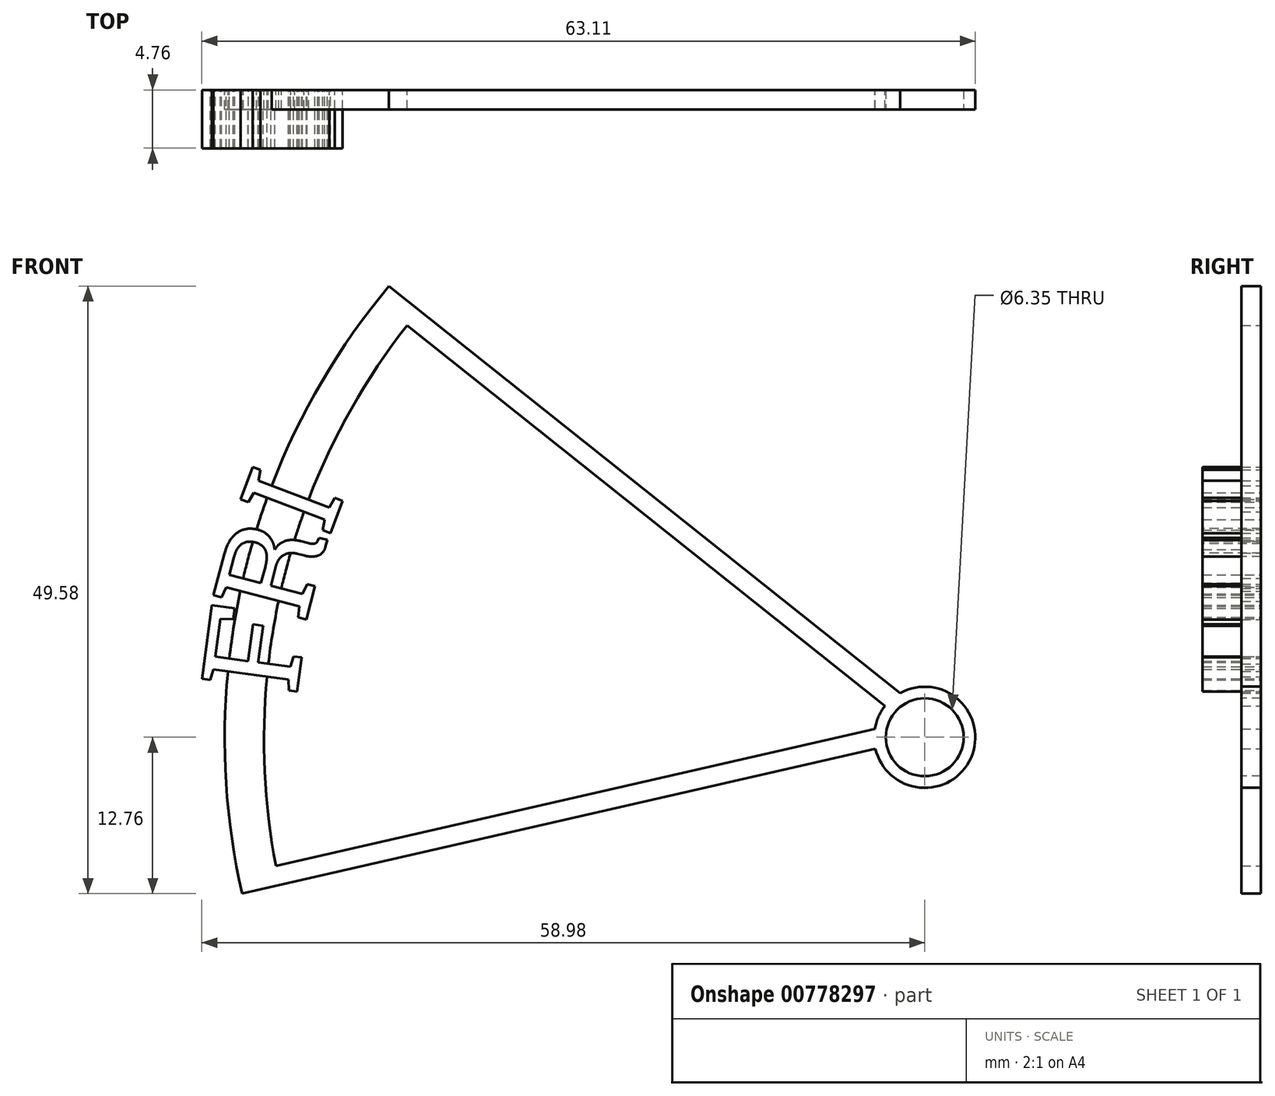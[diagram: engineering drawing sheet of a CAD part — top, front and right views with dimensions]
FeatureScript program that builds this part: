
annotation { "Feature Type Name" : "Feature", "Feature Type Description" : "" }
export const myFeature = defineFeature(function(context is Context, id is Id, definition is map)
    precondition{}
    {
        {
            var Q0;
            Q0=qCreatedBy(makeId("Front.planeOp"),FACE);
            var sketch = newSketch(context, id + "F0", { "sketchPlane" : qUnion([Q0])});
            skCircle(sketch, "E0", {"center": v(0, 0) * mm, "radius": 59.18 * mm, "construction": true});
            skCircle(sketch, "E1", {"center": v(0, 0) * mm, "radius": 50.8 * mm, "construction": true});
            skLineSegment(sketch, "E2", {"start": v(0, 0) * mm, "end": v(0, 59.18) * mm, "construction": true});
            skLineSegment(sketch, "E3", {"start": v(0, 0) * mm, "end": v(-57.83, -12.6) * mm, "construction": true});
            skLineSegment(sketch, "E4", {"start": v(0, 0) * mm, "end": v(-58.65, 7.93) * mm, "construction": true});
            skLineSegment(sketch, "E5", {"start": v(0, 0) * mm, "end": v(-57.24, 15.02) * mm, "construction": true});
            skLineSegment(sketch, "E6", {"start": v(0, 0) * mm, "end": v(-55.36, 20.92) * mm, "construction": true});
            skText(sketch, "E7", { "text": "F", "fontName": "RobotoSlab-Regular.ttf"});
            skText(sketch, "E8", { "text": "R", "fontName": "RobotoSlab-Regular.ttf"});
            skText(sketch, "E9", { "text": "I", "fontName": "RobotoSlab-Regular.ttf"});
            skLineSegment(sketch, "E10", {"start": v(0, 0) * mm, "end": v(-59.13, 4.4) * mm, "construction": true});
            skLineSegment(sketch, "E11", {"start": v(0, 0) * mm, "end": v(-54.67, 22.74) * mm, "construction": true});
            skLineSegment(sketch, "E12", {"start": v(0, 0) * mm, "end": v(-45.9, 37.35) * mm, "construction": true});
            const initialGuessF0  = {"E7": [-0.05126, 0.00334, 0.13406, 0.99097, 0.00794], "E8": [-0.05055, 0.00924, 0.25383, 0.96725, 0.00794], "E9": [-0.04862, 0.0163, 0.35354, 0.93542, 0.00794]};
            skSetInitialGuess(sketch, initialGuessF0);
            skSolve(sketch);
        }
        {
            var Q0;
            Q0=qSketchRegion(id+"F0",true);
            extrude(context, id + "F1", {"entities" : qUnion([Q0]), "depth" : 4.76 * mm, "offsetDistance" : 25.4 * mm});
        }
        {
            var Q0;
            Q0=qCreatedBy(makeId("Front.planeOp"),FACE);
            var sketch = newSketch(context, id + "F2", { "sketchPlane" : qUnion([Q0])});
            skCircle(sketch, "E13", {"center": v(0, 0) * mm, "radius": 57.15 * mm, "construction": true});
            skCircle(sketch, "E14", {"center": v(0, 0) * mm, "radius": 53.98 * mm, "construction": true});
            skCircle(sketch, "E15", {"center": v(0, 0) * mm, "radius": 4.13 * mm, "construction": true});
            skLineSegment(sketch, "E16", {"start": v(0, 0) * mm, "end": v(0, 57.15) * mm, "construction": true});
            skLineSegment(sketch, "E17", {"start": v(0, 0) * mm, "end": v(-55.7, -12.76) * mm, "construction": true});
            skLineSegment(sketch, "E18", {"start": v(0, 0) * mm, "end": v(-42.23, 33.61) * mm, "construction": true});
            skLineSegment(sketch, "E19", {"start": v(-43.7, 36.82) * mm, "end": v(-2, 3.61) * mm, "construction": true});
            skLineSegment(sketch, "E20", {"start": v(-52.94, -10.5) * mm, "end": v(-4.07, 0.7) * mm, "construction": true});
            skLineSegment(sketch, "E21", {"start": v(-42.23, 33.61) * mm, "end": v(-3.23, 2.57) * mm});
            skLineSegment(sketch, "E22", {"start": v(-55.7, -12.76) * mm, "end": v(-4.02, -0.92) * mm});
            skLineSegment(sketch, "E23", {"start": v(-52.94, -10.5) * mm, "end": v(-4.07, 0.7) * mm});
            skLineSegment(sketch, "E24", {"start": v(-43.7, 36.82) * mm, "end": v(-2, 3.61) * mm});
            skCircle(sketch, "E25", {"center": v(0, 0) * mm, "radius": 4.13 * mm});
            skArc(sketch, "E26", {"start": v(-42.23, 33.61) * mm, "mid": v(-52.36, 12.72) * mm, "end": v(-52.94, -10.5) * mm});
            skArc(sketch, "E27", {"start": v(-43.7, 36.82) * mm, "mid": v(-55.5, 13.43) * mm, "end": v(-55.7, -12.76) * mm});
            skSolve(sketch);
        }
        {
            var Q0;
            {var subQ3=sQuery(id+"F2.wireOp",EDGE,"E21");Q0=makeQuery(id+"F2.imprint","IMPRINT",FACE,{"disambiguationData":[TD([[makeQuery(id+"F2.imprint","IMPRINT",EDGE,{"derivedFrom":subQ3}),1.0]])]});}
            var Q1;
            {var subQ0=sQuery(id+"F2.wireOp",EDGE,"E25");var subQ1=makeQuery(id+"F2.imprint","INTERSECT",VERTEX,{"derivedFrom":[sQuery(id+"F2.wireOp",EDGE,"E21"),subQ0]});Q1=makeQuery(id+"F2.imprint","IMPRINT",FACE,{"disambiguationData":[TD([[makeQuery(id+"F2.imprint","IMPRINT",EDGE,{"disambiguationData":[TD([[subQ1,1.0]])],"derivedFrom":subQ0}),1.0]])]});}
            extrude(context, id + "F3", {"entities" : qUnion([Q0, Q1]), "operationType" : NewBodyOperationType.ADD, "depth" : 1.59 * mm, "offsetDistance" : 25.4 * mm});
        }
        {
            var Q0;
            {var subQ0=sQuery(id+"F2.wireOp",EDGE,"E22");var subQ1=sQuery(id+"F2.wireOp",EDGE,"E21");var subQ2=sQuery(id+"F2.wireOp",EDGE,"E25");var subQ3=sQuery(id+"F2.wireOp",EDGE,"E24");var subQ4=sQuery(id+"F2.wireOp",EDGE,"E23");var subQ5=sQuery(id+"F2.wireOp",EDGE,"E26");var subQ6=sQuery(id+"F2.wireOp",EDGE,"E27");Q0=makeQuery(id+"F3.boolean.opBoolean","SPLIT",FACE,{"disambiguationData":[TD([makeQuery(id+"F1.opExtrude","SWEPT_FACE",FACE,{"disambiguationData":[OSD([sQuery(id+"F0.wireOp",EDGE,"E7.sketch_text.stroke-1")])]})])],"derivedFrom":makeQuery(id+"F3.opExtrude","CAP_FACE",FACE,{"disambiguationData":[OSD([subQ1,subQ0,subQ4,subQ3,subQ2,subQ5,subQ6])],"isStart":false})});}
            var sketch = newSketch(context, id + "F4", { "sketchPlane" : qUnion([Q0])});
            skPoint(sketch, "E28", {"position": v(0, 0) * mm});
            skSolve(sketch);
        }
        {
            var Q0;
            Q0=sQuery(id+"F4.wireOp",VERTEX,"E28");
            var Q1;
            Q1=makeQuery(id+"F1.opExtrude","SWEPT_BODY",BODY,{"disambiguationData":[OSD([sQuery(id+"F0.wireOp",EDGE,"E7.sketch_text.stroke-0"),sQuery(id+"F0.wireOp",EDGE,"E7.sketch_text.stroke-1"),sQuery(id+"F0.wireOp",EDGE,"E7.sketch_text.stroke-2"),sQuery(id+"F0.wireOp",EDGE,"E7.sketch_text.stroke-3"),sQuery(id+"F0.wireOp",EDGE,"E7.sketch_text.stroke-4"),sQuery(id+"F0.wireOp",EDGE,"E7.sketch_text.stroke-5"),sQuery(id+"F0.wireOp",EDGE,"E7.sketch_text.stroke-6"),sQuery(id+"F0.wireOp",EDGE,"E7.sketch_text.stroke-7"),sQuery(id+"F0.wireOp",EDGE,"E7.sketch_text.stroke-8"),sQuery(id+"F0.wireOp",EDGE,"E7.sketch_text.stroke-9"),sQuery(id+"F0.wireOp",EDGE,"E7.sketch_text.stroke-10"),sQuery(id+"F0.wireOp",EDGE,"E7.sketch_text.stroke-11"),sQuery(id+"F0.wireOp",EDGE,"E7.sketch_text.stroke-12"),sQuery(id+"F0.wireOp",EDGE,"E7.sketch_text.stroke-13"),sQuery(id+"F0.wireOp",EDGE,"E7.sketch_text.stroke-14"),sQuery(id+"F0.wireOp",EDGE,"E7.sketch_text.stroke-15"),sQuery(id+"F0.wireOp",EDGE,"E7.sketch_text.stroke-16"),sQuery(id+"F0.wireOp",EDGE,"E7.sketch_text.stroke-17")])]});
            hole(context, id + "F5", {"style" : HoleStyle.SIMPLE, "endStyle" : HoleEndStyle.THROUGH, "holeDiameter" : 6.35 * mm, "majorDiameter" : 6.35 * mm, "isTappedThrough" : true, "tappedDepth" : 12.7 * mm, "tapClearance" : 3, "locations" : qUnion([Q0]), "scope" : qUnion([Q1])});
        }
    });
